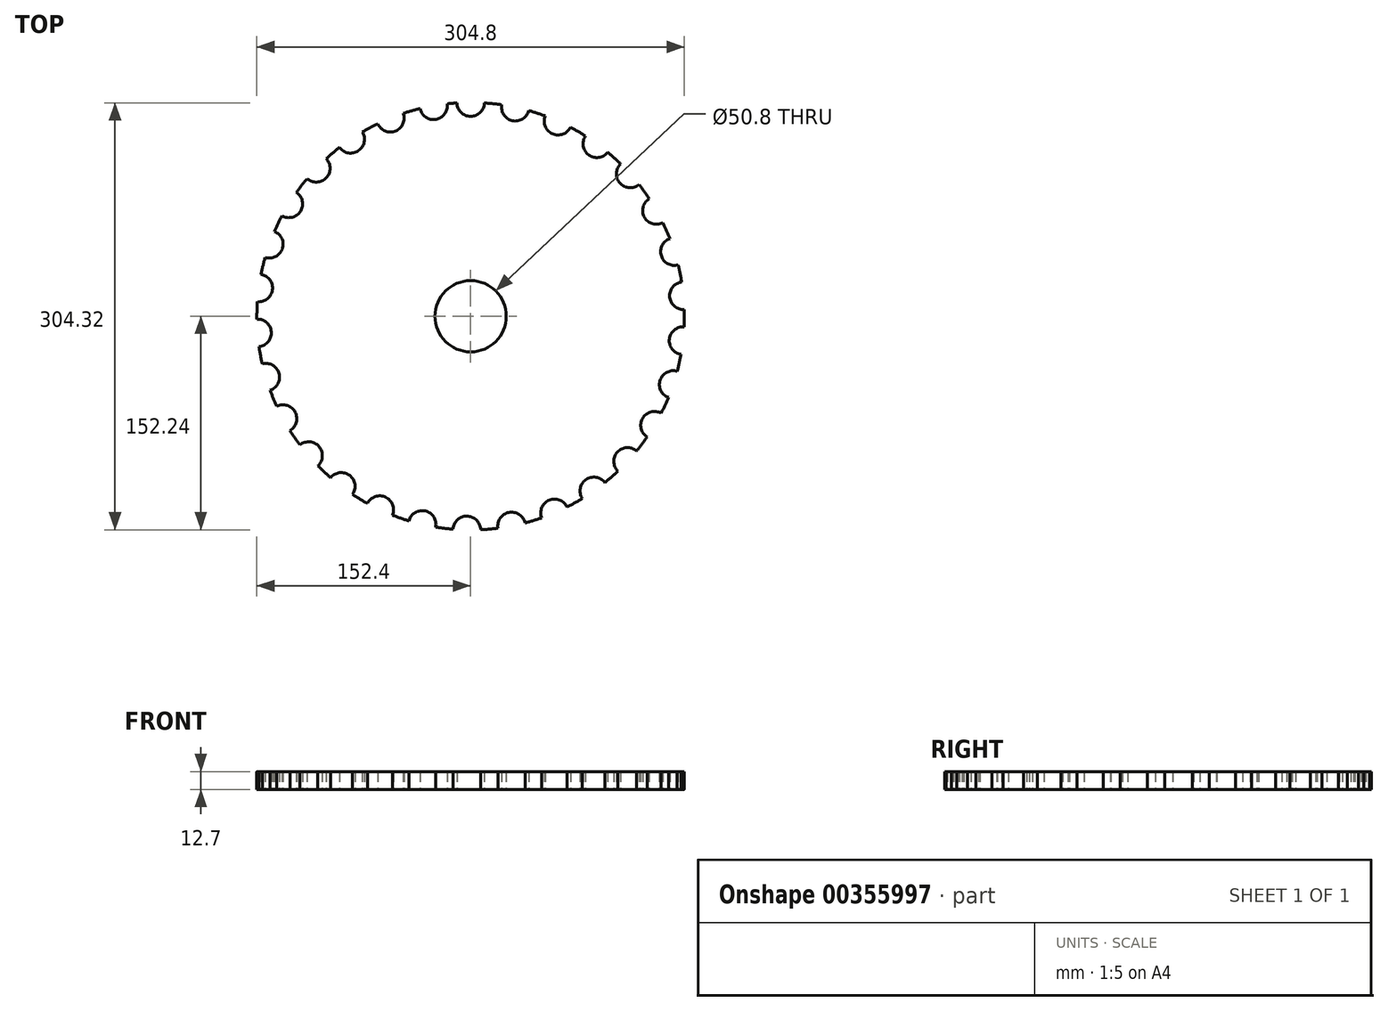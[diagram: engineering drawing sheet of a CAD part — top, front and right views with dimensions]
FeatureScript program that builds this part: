
annotation { "Feature Type Name" : "Feature", "Feature Type Description" : "" }
export const myFeature = defineFeature(function(context is Context, id is Id, definition is map)
    precondition{}
    {
        {
            var Q0;
            Q0=qCreatedBy(makeId("Top.planeOp"),FACE);
            var sketch = newSketch(context, id + "F0", { "sketchPlane" : qUnion([Q0])});
            skCircle(sketch, "E0", {"center": v(0, 0) * mm, "radius": 152.4 * mm});
            skCircle(sketch, "E1", {"center": v(0, 152.4) * mm, "radius": 9.83 * mm});
            skCircle(sketch, "E2.1.0", {"center": v(31.87, 149.03) * mm, "radius": 9.83 * mm});
            skCircle(sketch, "E2.2.0", {"center": v(62.32, 139.07) * mm, "radius": 9.83 * mm});
            skCircle(sketch, "E2.3.0", {"center": v(90.02, 122.97) * mm, "radius": 9.83 * mm});
            skCircle(sketch, "E2.4.0", {"center": v(113.74, 101.43) * mm, "radius": 9.83 * mm});
            skCircle(sketch, "E2.5.0", {"center": v(132.44, 75.4) * mm, "radius": 9.83 * mm});
            skCircle(sketch, "E2.6.0", {"center": v(145.28, 46.05) * mm, "radius": 9.83 * mm});
            skCircle(sketch, "E2.7.0", {"center": v(151.7, 14.65) * mm, "radius": 9.83 * mm});
            skCircle(sketch, "E2.8.0", {"center": v(151.4, -17.39) * mm, "radius": 9.83 * mm});
            skCircle(sketch, "E2.9.0", {"center": v(144.42, -48.66) * mm, "radius": 9.83 * mm});
            skCircle(sketch, "E2.10.0", {"center": v(131.06, -77.78) * mm, "radius": 9.83 * mm});
            skCircle(sketch, "E2.11.0", {"center": v(111.9, -103.47) * mm, "radius": 9.83 * mm});
            skCircle(sketch, "E2.12.0", {"center": v(87.79, -124.58) * mm, "radius": 9.83 * mm});
            skCircle(sketch, "E2.13.0", {"center": v(59.8, -140.18) * mm, "radius": 9.83 * mm});
            skCircle(sketch, "E2.14.0", {"center": v(29.17, -149.58) * mm, "radius": 9.83 * mm});
            skCircle(sketch, "E2.15.0", {"center": v(-2.75, -152.38) * mm, "radius": 9.83 * mm});
            skCircle(sketch, "E2.16.0", {"center": v(-34.55, -148.43) * mm, "radius": 9.83 * mm});
            skCircle(sketch, "E2.17.0", {"center": v(-64.82, -137.93) * mm, "radius": 9.83 * mm});
            skCircle(sketch, "E2.18.0", {"center": v(-92.23, -121.32) * mm, "radius": 9.83 * mm});
            skCircle(sketch, "E2.19.0", {"center": v(-115.56, -99.36) * mm, "radius": 9.83 * mm});
            skCircle(sketch, "E2.20.0", {"center": v(-133.78, -73) * mm, "radius": 9.83 * mm});
            skCircle(sketch, "E2.21.0", {"center": v(-146.08, -43.42) * mm, "radius": 9.83 * mm});
            skCircle(sketch, "E2.22.0", {"center": v(-151.93, -11.91) * mm, "radius": 9.83 * mm});
            skCircle(sketch, "E2.23.0", {"center": v(-151.07, 20.12) * mm, "radius": 9.83 * mm});
            skCircle(sketch, "E2.24.0", {"center": v(-143.52, 51.26) * mm, "radius": 9.83 * mm});
            skCircle(sketch, "E2.25.0", {"center": v(-129.63, 80.14) * mm, "radius": 9.83 * mm});
            skCircle(sketch, "E2.26.0", {"center": v(-110, 105.47) * mm, "radius": 9.83 * mm});
            skCircle(sketch, "E2.27.0", {"center": v(-85.52, 126.14) * mm, "radius": 9.83 * mm});
            skCircle(sketch, "E2.28.0", {"center": v(-57.26, 141.23) * mm, "radius": 9.83 * mm});
            skCircle(sketch, "E2.29.0", {"center": v(-26.46, 150.08) * mm, "radius": 9.83 * mm});
            skLineSegment(sketch, "E2.anchor1", {"start": v(0, 0) * mm, "end": v(0, 152.4) * mm, "construction": true});
            skLineSegment(sketch, "E2.anchor2", {"start": v(0, 0) * mm, "end": v(-26.46, 150.08) * mm, "construction": true});
            skCircle(sketch, "E3", {"center": v(0, 0) * mm, "radius": 25.4 * mm});
            skSolve(sketch);
        }
        {
            var Q0;
            {var subQ1=sQuery(id+"F0.wireOp",EDGE,"E0");var subQ14=sQuery(id+"F0.wireOp",EDGE,"E2.7.0");var subQ15=makeQuery(id+"F0.imprint","INTERSECT",VERTEX,{"disambiguationData":[OD(0.0)],"derivedFrom":[subQ1,subQ14]});Q0=makeQuery(id+"F0.imprint","IMPRINT",FACE,{"disambiguationData":[TD([[makeQuery(id+"F0.imprint","IMPRINT",EDGE,{"disambiguationData":[TD([[subQ15,-1.0]])],"derivedFrom":subQ1}),1.0]])]});}
            extrude(context, id + "F1", {"entities" : qUnion([Q0]), "depth" : 12.7 * mm});
        }
    });
